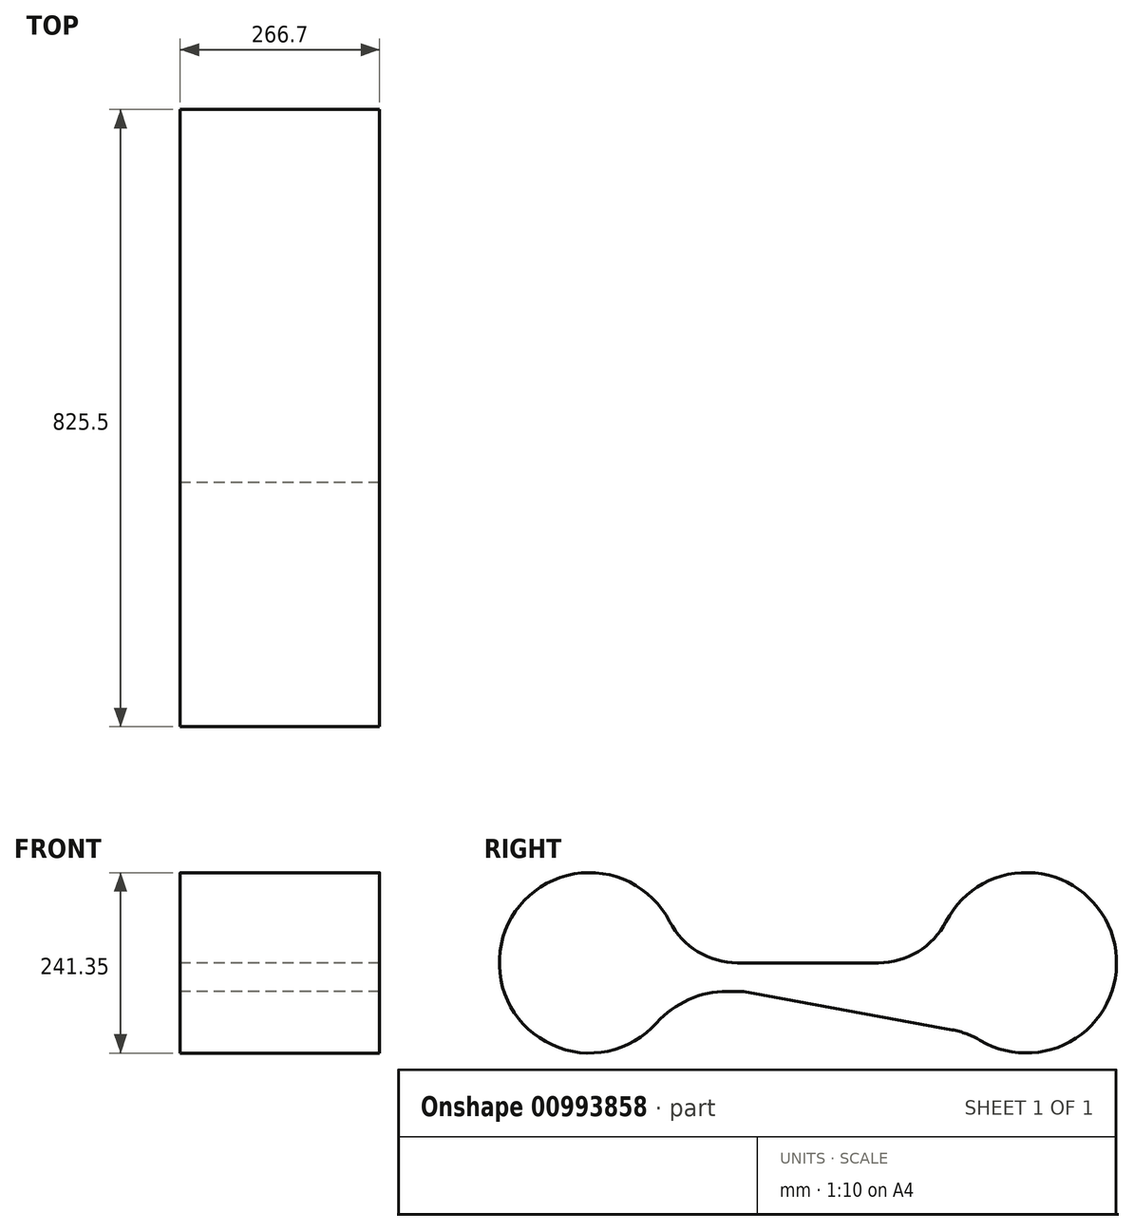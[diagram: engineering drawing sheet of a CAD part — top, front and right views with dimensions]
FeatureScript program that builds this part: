
annotation { "Feature Type Name" : "Feature", "Feature Type Description" : "" }
export const myFeature = defineFeature(function(context is Context, id is Id, definition is map)
    precondition{}
    {
        {
            var Q0;
            Q0=qCreatedBy(makeId("Right.planeOp"),FACE);
            var sketch = newSketch(context, id + "F0", { "sketchPlane" : qUnion([Q0])});
            skLineSegment(sketch, "E0", {"start": v(0, 0) * mm, "end": v(-94.43, 0) * mm});
            skLineSegment(sketch, "E1", {"start": v(0, 0) * mm, "end": v(94.43, 0) * mm});
            skArc(sketch, "E2.0", {"start": v(-184.8, 55.14) * mm, "mid": v(-411.77, 15.3) * mm, "end": v(-202.17, -80.45) * mm});
            skArc(sketch, "E3.0", {"start": v(230.51, -103.72) * mm, "mid": v(408.05, 33.4) * mm, "end": v(184.79, 55.17) * mm});
            skLineSegment(sketch, "E4", {"start": v(-85.9, -38.1) * mm, "end": v(192.92, -89.6) * mm});
            skLineSegment(sketch, "E5.0", {"start": v(-85.9, -38.1) * mm, "end": v(-107.5, -38.1) * mm});
            skPoint(sketch, "E6.orphan", {"position": v(292.1, -107.92) * mm});
            skPoint(sketch, "E7.visualSharp", {"position": v(-177.62, -38.12) * mm});
            skArc(sketch, "E7.filletArc", {"start": v(-107.5, -38.1) * mm, "mid": v(-159.36, -49.18) * mm, "end": v(-202.17, -80.45) * mm});
            skPoint(sketch, "E8.visualSharp", {"position": v(216.44, -93.95) * mm});
            skArc(sketch, "E8.filletArc", {"start": v(230.51, -103.72) * mm, "mid": v(212.34, -95) * mm, "end": v(192.92, -89.6) * mm});
            skPoint(sketch, "E9.visualSharp", {"position": v(-171.45, -0.01) * mm});
            skArc(sketch, "E9.filletArc", {"start": v(-184.8, 55.14) * mm, "mid": v(-147.37, 14.87) * mm, "end": v(-94.43, 0) * mm});
            skPoint(sketch, "E10.visualSharp", {"position": v(171.45, 0.02) * mm});
            skArc(sketch, "E10.filletArc", {"start": v(94.43, 0) * mm, "mid": v(147.36, 14.9) * mm, "end": v(184.79, 55.17) * mm});
            skSolve(sketch);
        }
        {
            var Q0;
            Q0=makeQuery(id+"F0.imprint","IMPRINT",FACE,{"disambiguationData":[TD([[makeQuery(id+"F0.imprint","IMPRINT",EDGE,{"derivedFrom":sQuery(id+"F0.wireOp",EDGE,"E0")}),1.0]])]});
            extrude(context, id + "F1", {"entities" : qUnion([Q0]), "depth" : 254 * mm, "offsetDistance" : 25.4 * mm, "hasSecondDirection" : true, "secondDirectionOppositeDirection" : true, "secondDirectionDepth" : 254 * mm});
        }
        {
            var Q0;
            Q0=makeQuery(id+"F1.opExtrude","CAP_FACE",FACE,{"disambiguationData":[OSD([sQuery(id+"F0.wireOp",EDGE,"E0"),sQuery(id+"F0.wireOp",EDGE,"E1"),sQuery(id+"F0.wireOp",EDGE,"E2.0"),sQuery(id+"F0.wireOp",EDGE,"E3.0"),sQuery(id+"F0.wireOp",EDGE,"E4"),sQuery(id+"F0.wireOp",EDGE,"E5.0"),sQuery(id+"F0.wireOp",EDGE,"E7.filletArc"),sQuery(id+"F0.wireOp",EDGE,"E8.filletArc"),sQuery(id+"F0.wireOp",EDGE,"E9.filletArc"),sQuery(id+"F0.wireOp",EDGE,"E10.filletArc")])],"isStart":false});
            var sketch = newSketch(context, id + "F2", { "sketchPlane" : qUnion([Q0])});
            skLineSegment(sketch, "E11", {"start": v(0, 0) * mm, "end": v(-292.1, -0.02) * mm});
            skCircle(sketch, "E12", {"center": v(-292.1, -0.02) * mm, "radius": 120.65 * mm});
            skCircle(sketch, "E13", {"center": v(292.1, 0.03) * mm, "radius": 120.65 * mm});
            skLineSegment(sketch, "E14.bottom", {"start": v(-265.27, 92.49) * mm, "end": v(264.63, 92.49) * mm});
            skLineSegment(sketch, "E14.top", {"start": v(-265.27, -117.45) * mm, "end": v(264.63, -117.45) * mm});
            skLineSegment(sketch, "E14.left", {"start": v(-265.27, 92.49) * mm, "end": v(-265.27, -117.45) * mm});
            skLineSegment(sketch, "E14.right", {"start": v(264.63, 92.49) * mm, "end": v(264.63, -117.45) * mm});
            skSolve(sketch);
        }
        {
            var Q0;
            Q0=qSketchRegion(id+"F2",true);
            extrude(context, id + "F3", {"entities" : qUnion([Q0]), "operationType" : NewBodyOperationType.REMOVE, "oppositeDirection" : true, "depth" : 120.65 * mm, "offsetDistance" : 25.4 * mm});
        }
        {
            var Q0;
            Q0=makeQuery(id+"F1.opExtrude","CAP_FACE",FACE,{"disambiguationData":[OSD([sQuery(id+"F0.wireOp",EDGE,"E0"),sQuery(id+"F0.wireOp",EDGE,"E1"),sQuery(id+"F0.wireOp",EDGE,"E2.0"),sQuery(id+"F0.wireOp",EDGE,"E3.0"),sQuery(id+"F0.wireOp",EDGE,"E4"),sQuery(id+"F0.wireOp",EDGE,"E5.0"),sQuery(id+"F0.wireOp",EDGE,"E7.filletArc"),sQuery(id+"F0.wireOp",EDGE,"E8.filletArc"),sQuery(id+"F0.wireOp",EDGE,"E9.filletArc"),sQuery(id+"F0.wireOp",EDGE,"E10.filletArc")])],"isStart":true});
            var sketch = newSketch(context, id + "F4", { "sketchPlane" : qUnion([Q0])});
            skCircle(sketch, "E15", {"center": v(-292.1, 0.03) * mm, "radius": 120.65 * mm});
            skCircle(sketch, "E16", {"center": v(292.1, -0.02) * mm, "radius": 120.65 * mm});
            skLineSegment(sketch, "E17.bottom", {"start": v(-248.59, 112.56) * mm, "end": v(286.2, 112.56) * mm});
            skLineSegment(sketch, "E17.top", {"start": v(-248.59, -112.58) * mm, "end": v(286.2, -112.58) * mm});
            skLineSegment(sketch, "E17.left", {"start": v(-248.59, 112.56) * mm, "end": v(-248.59, -112.58) * mm});
            skLineSegment(sketch, "E17.right", {"start": v(286.2, 112.56) * mm, "end": v(286.2, -112.58) * mm});
            skSolve(sketch);
        }
        {
            var Q0;
            Q0=qSketchRegion(id+"F4",true);
            extrude(context, id + "F5", {"entities" : qUnion([Q0]), "operationType" : NewBodyOperationType.REMOVE, "oppositeDirection" : true, "depth" : 120.65 * mm, "offsetDistance" : 25.4 * mm});
        }
    });
